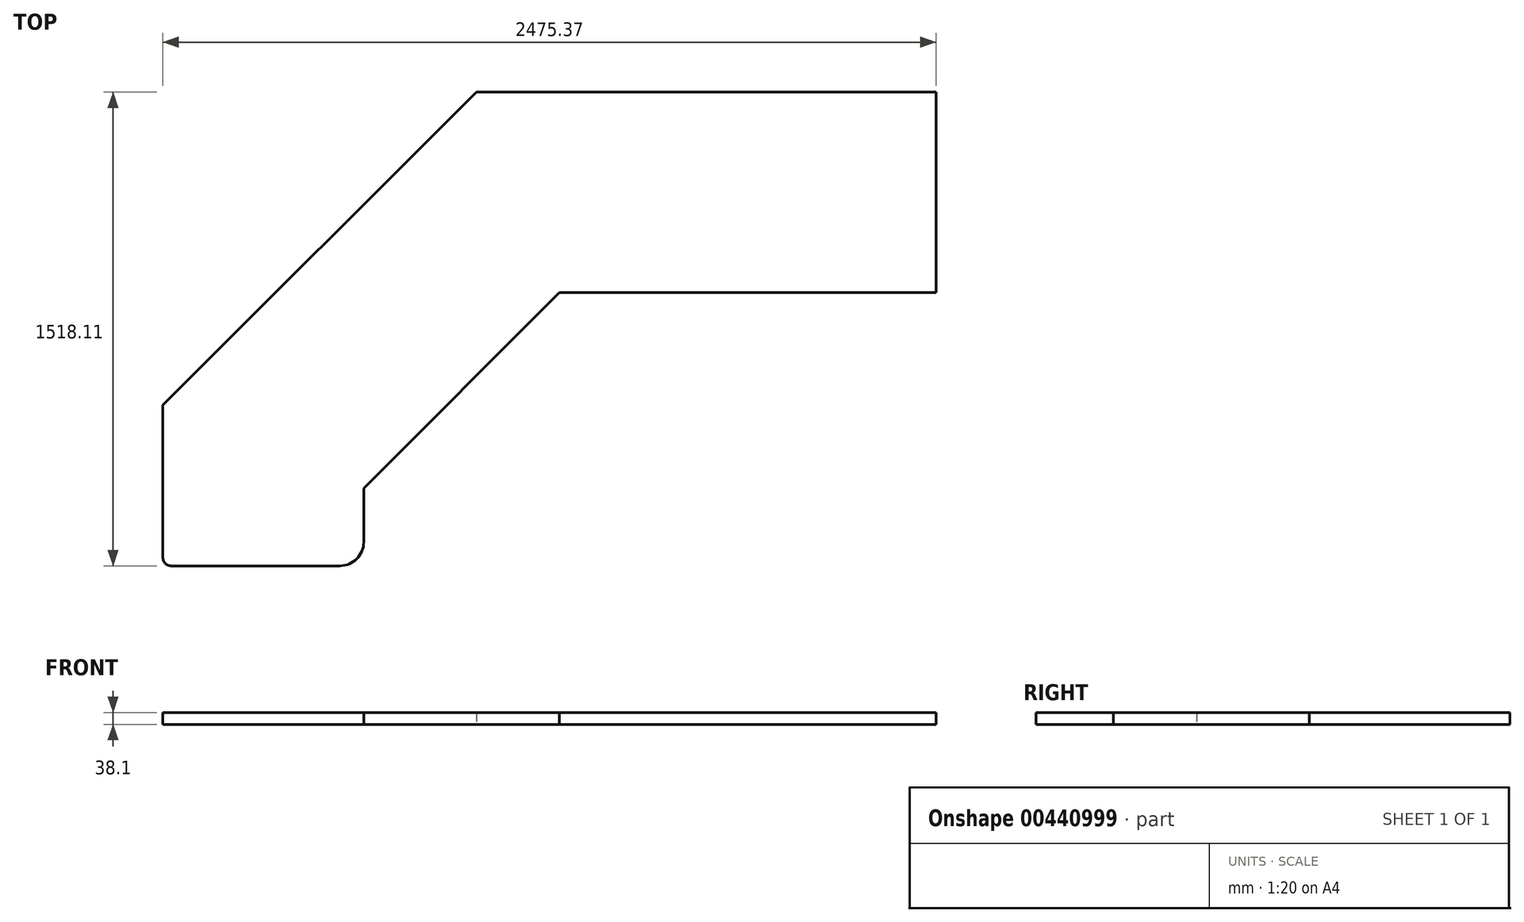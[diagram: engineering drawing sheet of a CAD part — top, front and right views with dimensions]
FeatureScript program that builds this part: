
annotation { "Feature Type Name" : "Feature", "Feature Type Description" : "" }
export const myFeature = defineFeature(function(context is Context, id is Id, definition is map)
    precondition{}
    {
        {
            var Q0;
            Q0=qCreatedBy(makeId("Top.planeOp"),FACE);
            var sketch = newSketch(context, id + "F0", { "sketchPlane" : qUnion([Q0])});
            skLineSegment(sketch, "E0", {"start": v(0, 0) * mm, "end": v(-1471.7, 0) * mm});
            skLineSegment(sketch, "E1", {"start": v(-1471.7, 0) * mm, "end": v(-2475.37, -1003.67) * mm});
            skLineSegment(sketch, "E2", {"start": v(-2475.37, -1003.67) * mm, "end": v(-2475.37, -1518.1) * mm});
            skLineSegment(sketch, "E3", {"start": v(-2475.37, -1518.1) * mm, "end": v(-1832.43, -1518.1) * mm});
            skLineSegment(sketch, "E4", {"start": v(-1832.43, -1518.1) * mm, "end": v(-1832.43, -1269.98) * mm});
            skLineSegment(sketch, "E5", {"start": v(-1832.43, -1269.98) * mm, "end": v(-1205.39, -642.94) * mm});
            skLineSegment(sketch, "E6", {"start": v(-1205.39, -642.94) * mm, "end": v(0, -642.94) * mm});
            skLineSegment(sketch, "E7", {"start": v(0, -642.94) * mm, "end": v(0, 0) * mm});
            skSolve(sketch);
        }
        {
            var Q0;
            Q0=makeQuery(id+"F0.imprint","IMPRINT",FACE,{"disambiguationData":[TD([[makeQuery(id+"F0.imprint","IMPRINT",EDGE,{"derivedFrom":sQuery(id+"F0.wireOp",EDGE,"E0")}),1.0]])]});
            extrude(context, id + "F1", {"entities" : qUnion([Q0]), "depth" : 38.1 * mm});
        }
        {
            var Q0;
            Q0=makeQuery(id+"F1.opExtrude","SWEPT_EDGE",EDGE,{"disambiguationData":[OSD([sQuery(id+"F0.wireOp",EDGE,"E3"),sQuery(id+"F0.wireOp",EDGE,"E4")])]});
            fillet(context, id + "F2", {"entities" : qUnion([Q0]), "radius" : 76.2 * mm, "tangentPropagation" : true, "allowEdgeOverflow" : false});
        }
        {
            var Q0;
            Q0=makeQuery(id+"F1.opExtrude","SWEPT_EDGE",EDGE,{"disambiguationData":[OSD([sQuery(id+"F0.wireOp",EDGE,"E2"),sQuery(id+"F0.wireOp",EDGE,"E3")])]});
            fillet(context, id + "F3", {"entities" : qUnion([Q0]), "radius" : 25.4 * mm, "tangentPropagation" : true, "allowEdgeOverflow" : false});
        }
    });
